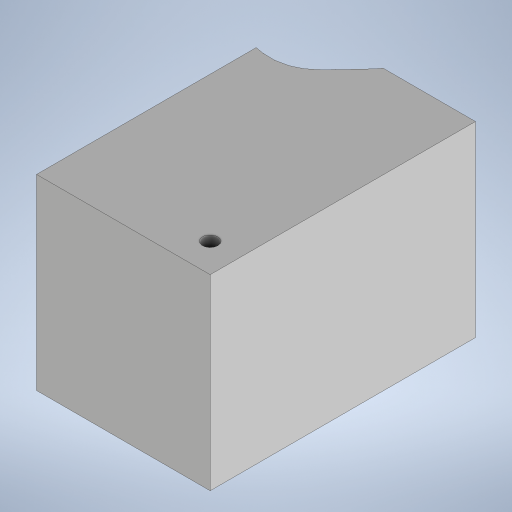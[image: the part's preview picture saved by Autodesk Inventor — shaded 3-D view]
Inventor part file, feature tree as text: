
AUTODESK INVENTOR PART (.ipt)
format: ipt  version: 2024 (Build 280153000, 153)  size: 10,638,848 bytes
history: native  units: mm
features: other x6, sketch x6, extrude x5, plane x2
ambient origin geometry x8: Origin, YZ Plane, XZ Plane, XY Plane, X Axis, Y Axis, Z Axis, Center Point
bodies: Body1 (feature_tree)
feature tree (19):
  other  "M.ipt"
  plane  "Plano de trabajo1"
  extrude  "Extrusión1"  [1 undecoded]
  other  "Combinar1"
  sketch  "Boceto3"  dims[d2=550.0mm d3=520.0mm]
  sketch  "Boceto4"  dims[d4=550.0mm d5=0.0mm d6=129.8482mm]
  plane  "Plano de trabajo2"
  sketch  "Boceto5"  dims[d17=180.0mm d18=180.0mm]
  extrude  "Extrusión2"  Depth=520.0mm
  extrude  "Extrusión3"  Depth=129.8482mm
  extrude  "Extrusión4"  Depth=180.0mm
  extrude  "Extrusión5"  Depth=180.0mm
  other  "Sólido1::M.ipt"
  other  "OperaciónIdentificador1"
  sketch  "Boceto1"  dims[d0=25.0mm d1=-365.0mm]
  other  "Sólido2"
  sketch  "Boceto6"  dims[d22=326.0mm d23=180.0mm]
  sketch  "Boceto7"  dims[d24=180.0mm d25=180.0mm d26=10.0mm d27=0.0mm d28=1000.0mm d29=0.0mm d30=30.0mm d31=30.0mm d32=16.0mm d33=16.0mm d34=0.0mm d35=30.0mm d36=30.0mm d37=16.0mm d38=16.0mm d39=0.0mm d14=0.5mm d15=0.872665mm d16=0.5mm d19=0.5mm d20=0.872665mm d21=0.5mm]
  other  "Sólido1"
note: 1 required parameter value undecoded (feature->parameter linkage not recoverable at this tier; creation-order binding heuristic only, values carry confidence <= 0.55)
